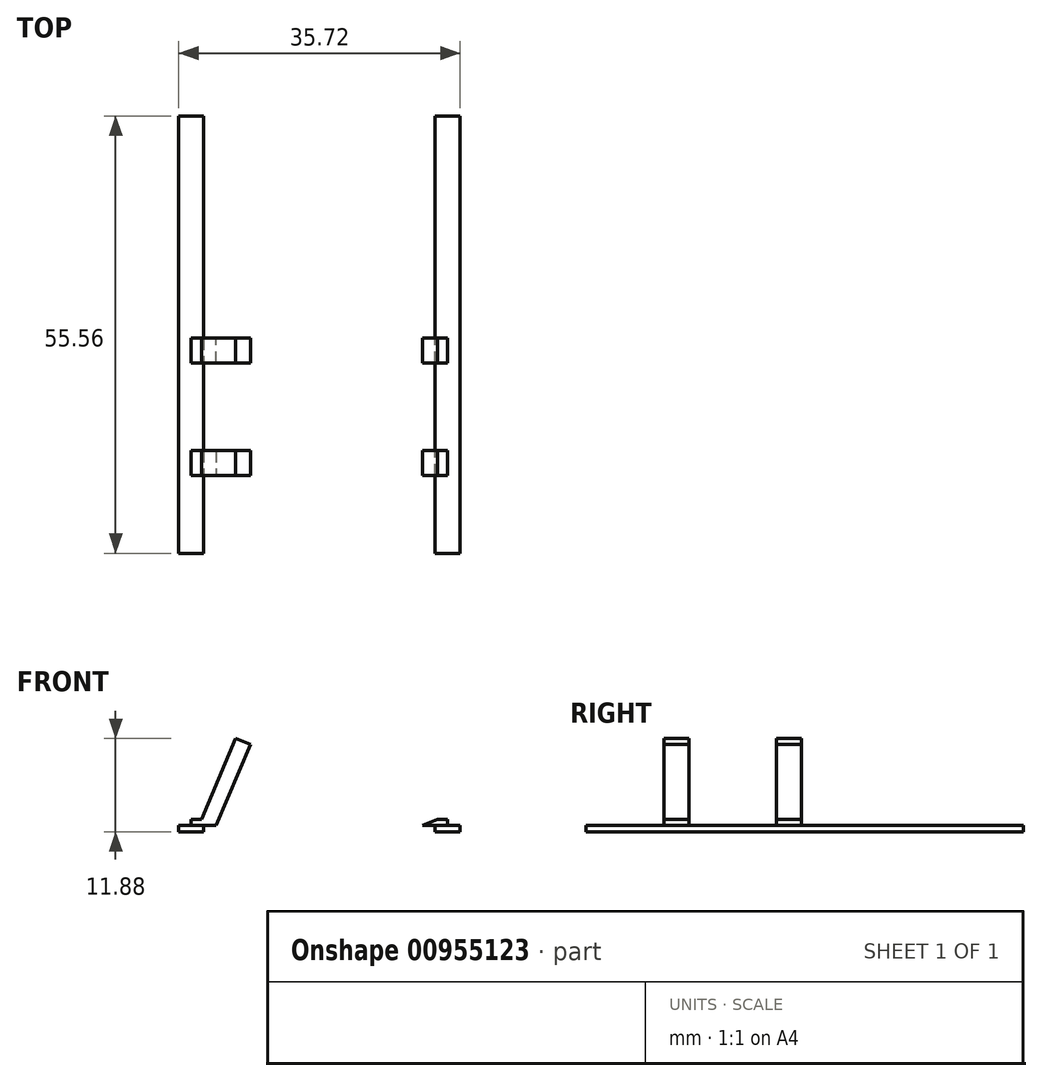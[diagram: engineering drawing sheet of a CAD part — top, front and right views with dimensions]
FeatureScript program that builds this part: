
annotation { "Feature Type Name" : "Feature", "Feature Type Description" : "" }
export const myFeature = defineFeature(function(context is Context, id is Id, definition is map)
    precondition{}
    {
        {
            var Q0;
            Q0=qCreatedBy(makeId("Top.planeOp"),FACE);
            var sketch = newSketch(context, id + "F0", { "sketchPlane" : qUnion([Q0])});
            skLineSegment(sketch, "E0.bottom", {"start": v(-50.8, 83.67) * mm, "end": v(-47.62, 83.67) * mm});
            skLineSegment(sketch, "E0.top", {"start": v(-50.8, 28.11) * mm, "end": v(-47.62, 28.11) * mm});
            skLineSegment(sketch, "E0.left", {"start": v(-50.8, 83.67) * mm, "end": v(-50.8, 28.11) * mm});
            skLineSegment(sketch, "E0.right", {"start": v(-47.62, 83.67) * mm, "end": v(-47.62, 28.11) * mm});
            skLineSegment(sketch, "E1.bottom", {"start": v(-15.08, 28.11) * mm, "end": v(-18.25, 28.11) * mm});
            skLineSegment(sketch, "E1.top", {"start": v(-15.08, 83.67) * mm, "end": v(-18.25, 83.67) * mm});
            skLineSegment(sketch, "E1.left", {"start": v(-15.08, 28.11) * mm, "end": v(-15.08, 83.67) * mm});
            skLineSegment(sketch, "E1.right", {"start": v(-18.25, 28.11) * mm, "end": v(-18.25, 83.67) * mm});
            skSolve(sketch);
        }
        {
            var Q0;
            Q0=makeQuery(id+"F0.imprint","IMPRINT",FACE,{"disambiguationData":[TD([[makeQuery(id+"F0.imprint","IMPRINT",EDGE,{"derivedFrom":sQuery(id+"F0.wireOp",EDGE,"E1.bottom")}),-1.0]])]});
            var Q1;
            Q1=makeQuery(id+"F0.imprint","IMPRINT",FACE,{"disambiguationData":[TD([[makeQuery(id+"F0.imprint","IMPRINT",EDGE,{"derivedFrom":sQuery(id+"F0.wireOp",EDGE,"E0.bottom")}),-1.0]])]});
            extrude(context, id + "F1", {"entities" : qUnion([Q0, Q1]), "depth" : 0.8 * mm, "offsetDistance" : 25.4 * mm});
        }
        {
            var Q0;
            Q0=makeQuery(id+"F1.opExtrude","CAP_FACE",FACE,{"disambiguationData":[OSD([sQuery(id+"F0.wireOp",EDGE,"E0.bottom"),sQuery(id+"F0.wireOp",EDGE,"E0.top"),sQuery(id+"F0.wireOp",EDGE,"E0.left"),sQuery(id+"F0.wireOp",EDGE,"E0.right")])],"isStart":false});
            var sketch = newSketch(context, id + "F2", { "sketchPlane" : qUnion([Q0])});
            skPoint(sketch, "E2.oppositeSnap0", {"position": v(-49.21, 28.11) * mm});
            skLineSegment(sketch, "E2.bottom", {"start": v(-46.04, 41.16) * mm, "end": v(-49.21, 41.16) * mm});
            skLineSegment(sketch, "E2.top", {"start": v(-46.04, 37.99) * mm, "end": v(-49.21, 37.99) * mm});
            skLineSegment(sketch, "E2.left", {"start": v(-46.04, 41.16) * mm, "end": v(-46.04, 37.99) * mm});
            skLineSegment(sketch, "E2.right", {"start": v(-49.21, 41.16) * mm, "end": v(-49.21, 37.99) * mm});
            skLineSegment(sketch, "E3.bottom", {"start": v(-46.04, 52.28) * mm, "end": v(-49.21, 52.28) * mm});
            skLineSegment(sketch, "E3.top", {"start": v(-46.04, 55.45) * mm, "end": v(-49.21, 55.45) * mm});
            skLineSegment(sketch, "E3.left", {"start": v(-46.04, 52.28) * mm, "end": v(-46.04, 55.45) * mm});
            skLineSegment(sketch, "E3.right", {"start": v(-49.21, 52.28) * mm, "end": v(-49.21, 55.45) * mm});
            skLineSegment(sketch, "E4.bottom", {"start": v(-19.84, 37.99) * mm, "end": v(-16.67, 37.99) * mm});
            skLineSegment(sketch, "E4.top", {"start": v(-19.84, 41.16) * mm, "end": v(-16.67, 41.16) * mm});
            skLineSegment(sketch, "E4.left", {"start": v(-19.84, 37.99) * mm, "end": v(-19.84, 41.16) * mm});
            skLineSegment(sketch, "E4.right", {"start": v(-16.67, 37.99) * mm, "end": v(-16.67, 41.16) * mm});
            skLineSegment(sketch, "E5.bottom", {"start": v(-19.84, 52.28) * mm, "end": v(-16.67, 52.28) * mm});
            skLineSegment(sketch, "E5.top", {"start": v(-19.84, 55.45) * mm, "end": v(-16.67, 55.45) * mm});
            skLineSegment(sketch, "E5.left", {"start": v(-19.84, 52.28) * mm, "end": v(-19.84, 55.45) * mm});
            skLineSegment(sketch, "E5.right", {"start": v(-16.67, 52.28) * mm, "end": v(-16.67, 55.45) * mm});
            skSolve(sketch);
        }
        {
            var Q0;
            {var subQ0=sQuery(id+"F2.wireOp",EDGE,"E3.right");Q0=makeQuery(id+"F2.imprint","IMPRINT",FACE,{"disambiguationData":[TD([[makeQuery(id+"F2.imprint","IMPRINT",EDGE,{"derivedFrom":subQ0}),-1.0]])]});}
            var Q1;
            {var subQ0=sQuery(id+"F2.wireOp",EDGE,"E3.left");Q1=makeQuery(id+"F2.imprint","IMPRINT",FACE,{"disambiguationData":[TD([[makeQuery(id+"F2.imprint","IMPRINT",EDGE,{"derivedFrom":subQ0}),1.0]])]});}
            var Q2;
            {var subQ0=sQuery(id+"F2.wireOp",EDGE,"E2.right");Q2=makeQuery(id+"F2.imprint","IMPRINT",FACE,{"disambiguationData":[TD([[makeQuery(id+"F2.imprint","IMPRINT",EDGE,{"derivedFrom":subQ0}),1.0]])]});}
            var Q3;
            {var subQ0=sQuery(id+"F2.wireOp",EDGE,"E2.left");Q3=makeQuery(id+"F2.imprint","IMPRINT",FACE,{"disambiguationData":[TD([[makeQuery(id+"F2.imprint","IMPRINT",EDGE,{"derivedFrom":subQ0}),-1.0]])]});}
            var Q4;
            Q4=makeQuery(id+"F2.imprint","IMPRINT",FACE,{"disambiguationData":[TD([[makeQuery(id+"F2.imprint","IMPRINT",EDGE,{"derivedFrom":sQuery(id+"F2.wireOp",EDGE,"E5.bottom")}),1.0]])]});
            var Q5;
            Q5=makeQuery(id+"F2.imprint","IMPRINT",FACE,{"disambiguationData":[TD([[makeQuery(id+"F2.imprint","IMPRINT",EDGE,{"derivedFrom":sQuery(id+"F2.wireOp",EDGE,"E4.bottom")}),1.0]])]});
            extrude(context, id + "F3", {"entities" : qUnion([Q0, Q1, Q2, Q3, Q4, Q5]), "depth" : 0.8 * mm, "offsetDistance" : 25.4 * mm});
        }
        {
            var Q0;
            Q0=makeQuery(id+"F3.opExtrude","SWEPT_FACE",FACE,{"disambiguationData":[OSD([sQuery(id+"F2.wireOp",EDGE,"E2.top")])]});
            var sketch = newSketch(context, id + "F4", { "sketchPlane" : qUnion([Q0])});
            skLineSegment(sketch, "E6", {"start": v(-46.04, 0.8) * mm, "end": v(-47.92, 1.59) * mm});
            skSolve(sketch);
        }
        {
            var Q0;
            {var subQ0=sQuery(id+"F4.wireOp",EDGE,"E6");Q0=makeQuery(id+"F4.imprint","IMPRINT",FACE,{"disambiguationData":[TD([[makeQuery(id+"F4.imprint","IMPRINT",EDGE,{"derivedFrom":subQ0}),-1.0]])]});}
            extrude(context, id + "F5", {"entities" : qUnion([Q0]), "operationType" : NewBodyOperationType.REMOVE, "oppositeDirection" : true, "depth" : 25.4 * mm, "offsetDistance" : 25.4 * mm});
        }
        {
            var Q0;
            Q0=makeQuery(id+"F3.opExtrude","SWEPT_FACE",FACE,{"disambiguationData":[OSD([sQuery(id+"F2.wireOp",EDGE,"E4.bottom")])]});
            var sketch = newSketch(context, id + "F6", { "sketchPlane" : qUnion([Q0])});
            skLineSegment(sketch, "E7", {"start": v(-19.84, 0.8) * mm, "end": v(-17.96, 1.59) * mm});
            skSolve(sketch);
        }
        {
            var Q0;
            {var subQ0=sQuery(id+"F6.wireOp",EDGE,"E7");Q0=makeQuery(id+"F6.imprint","IMPRINT",FACE,{"disambiguationData":[TD([[makeQuery(id+"F6.imprint","IMPRINT",EDGE,{"derivedFrom":subQ0}),1.0]])]});}
            extrude(context, id + "F7", {"entities" : qUnion([Q0]), "operationType" : NewBodyOperationType.REMOVE, "oppositeDirection" : true, "depth" : 25.4 * mm, "offsetDistance" : 25.4 * mm});
        }
        {
            var Q0;
            {var subQ0=sQuery(id+"F2.wireOp",EDGE,"E3.bottom");Q0=makeQuery(id+"F5.boolean.opBoolean","COPY",FACE,{"disambiguationData":[TD([makeQuery(id+"F3.opExtrude","SWEPT_FACE",FACE,{"disambiguationData":[OSD([subQ0])]})])],"derivedFrom":makeQuery(id+"F5.opExtrude","SWEPT_FACE",FACE,{"disambiguationData":[OSD([sQuery(id+"F4.wireOp",EDGE,"E6")])]})});}
            var Q1;
            {var subQ0=sQuery(id+"F2.wireOp",EDGE,"E2.bottom");Q1=makeQuery(id+"F5.boolean.opBoolean","COPY",FACE,{"disambiguationData":[TD([makeQuery(id+"F3.opExtrude","SWEPT_FACE",FACE,{"disambiguationData":[OSD([subQ0])]})])],"derivedFrom":makeQuery(id+"F5.opExtrude","SWEPT_FACE",FACE,{"disambiguationData":[OSD([sQuery(id+"F4.wireOp",EDGE,"E6")])]})});}
            extrude(context, id + "F8", {"entities" : qUnion([Q0, Q1]), "operationType" : NewBodyOperationType.ADD, "depth" : 11.18 * mm, "offsetDistance" : 25.4 * mm});
        }
    });
